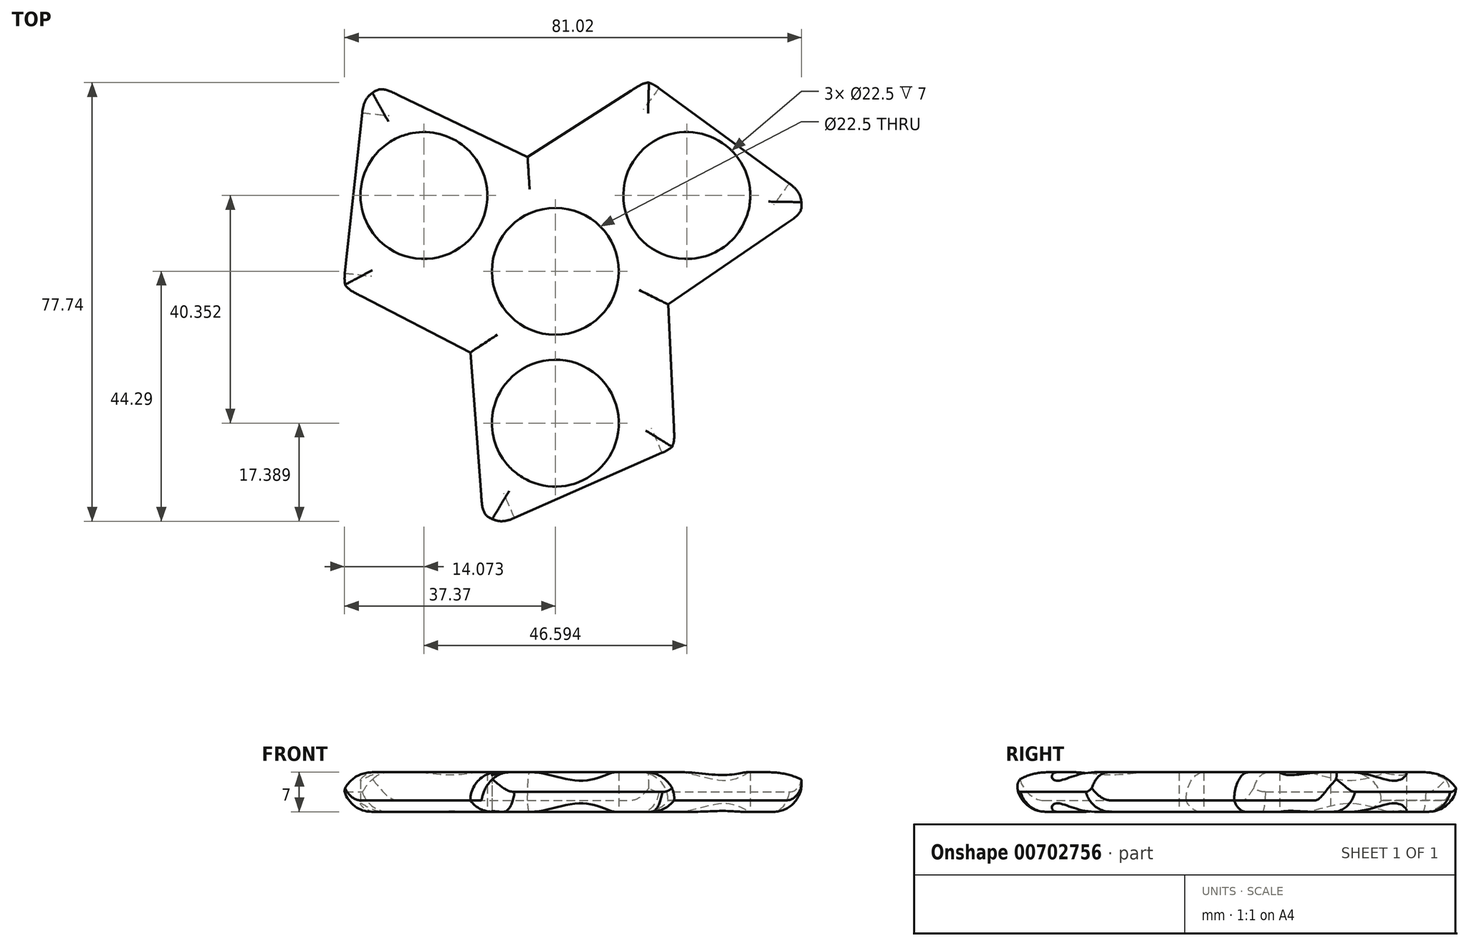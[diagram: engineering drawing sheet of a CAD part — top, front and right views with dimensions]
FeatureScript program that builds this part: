
annotation { "Feature Type Name" : "Feature", "Feature Type Description" : "" }
export const myFeature = defineFeature(function(context is Context, id is Id, definition is map)
    precondition{}
    {
        {
            var Q0;
            Q0=qCreatedBy(makeId("Top.planeOp"),FACE);
            var sketch = newSketch(context, id + "F0", { "sketchPlane" : qUnion([Q0])});
            skCircle(sketch, "E0", {"center": v(0, 0) * mm, "radius": 11.25 * mm});
            skLineSegment(sketch, "E1", {"start": v(19.99, -5.86) * mm, "end": v(21.2, -31.4) * mm});
            skCircle(sketch, "E2", {"center": v(0, -26.9) * mm, "radius": 11.25 * mm});
            skCircle(sketch, "E3.1.0", {"center": v(23.3, 13.45) * mm, "radius": 11.25 * mm});
            skLineSegment(sketch, "E3.1.1", {"start": v(-4.92, 20.24) * mm, "end": v(16.6, 34.06) * mm});
            skCircle(sketch, "E3.2.0", {"center": v(-23.3, 13.45) * mm, "radius": 11.25 * mm});
            skLineSegment(sketch, "E3.2.1", {"start": v(-15.07, -14.38) * mm, "end": v(-37.8, -2.65) * mm});
            skLineSegment(sketch, "E4", {"start": v(-37.8, -2.65) * mm, "end": v(-33.81, 34.11) * mm});
            skLineSegment(sketch, "E5.1.0", {"start": v(21.2, -31.4) * mm, "end": v(-12.64, -46.34) * mm});
            skLineSegment(sketch, "E5.2.0", {"start": v(16.6, 34.06) * mm, "end": v(46.45, 12.23) * mm});
            skLineSegment(sketch, "E6", {"start": v(-33.81, 34.11) * mm, "end": v(-4.92, 20.24) * mm});
            skLineSegment(sketch, "E7.1.0", {"start": v(-12.64, -46.34) * mm, "end": v(-15.07, -14.38) * mm});
            skLineSegment(sketch, "E7.2.0", {"start": v(46.45, 12.23) * mm, "end": v(19.99, -5.86) * mm});
            skSolve(sketch);
        }
        {
            var Q0;
            Q0 = qSketchRegion(id + "F0", true);
            extrude(context, id + "F1", {"entities" : qUnion([Q0]), "depth" : 7 * mm, "offsetDistance" : 25 * mm});
        }
        {
            var Q0;
            Q0=makeQuery(id+"F1.opExtrude","CAP_EDGE",EDGE,{"disambiguationData":[OSD([sQuery(id+"F0.wireOp",EDGE,"E4")])],"isStart":false});
            var Q1;
            Q1=makeQuery(id+"F1.opExtrude","CAP_EDGE",EDGE,{"disambiguationData":[OSD([sQuery(id+"F0.wireOp",EDGE,"E5.2.0")])],"isStart":false});
            var Q2;
            Q2=makeQuery(id+"F1.opExtrude","CAP_EDGE",EDGE,{"disambiguationData":[OSD([sQuery(id+"F0.wireOp",EDGE,"E5.1.0")])],"isStart":false});
            var Q3;
            Q3=makeQuery(id+"F1.opExtrude","CAP_EDGE",EDGE,{"disambiguationData":[OSD([sQuery(id+"F0.wireOp",EDGE,"E5.1.0")])],"isStart":true});
            var Q4;
            Q4=makeQuery(id+"F1.opExtrude","CAP_EDGE",EDGE,{"disambiguationData":[OSD([sQuery(id+"F0.wireOp",EDGE,"E4")])],"isStart":true});
            var Q5;
            Q5=makeQuery(id+"F1.opExtrude","CAP_EDGE",EDGE,{"disambiguationData":[OSD([sQuery(id+"F0.wireOp",EDGE,"E5.2.0")])],"isStart":true});
            fillet(context, id + "F2", {"entities" : qUnion([Q0, Q1, Q2, Q3, Q4, Q5]), "radius" : 5 * mm, "tangentPropagation" : true, "allowEdgeOverflow" : false});
        }
        {
            var Q0;
            Q0=makeQuery(id+"F1.opExtrude","CAP_EDGE",EDGE,{"disambiguationData":[OSD([sQuery(id+"F0.wireOp",EDGE,"E6")])],"isStart":false});
            var Q1;
            Q1=makeQuery(id+"F1.opExtrude","CAP_EDGE",EDGE,{"disambiguationData":[OSD([sQuery(id+"F0.wireOp",EDGE,"E3.1.1")])],"isStart":false});
            var Q2;
            Q2=makeQuery(id+"F1.opExtrude","CAP_EDGE",EDGE,{"disambiguationData":[OSD([sQuery(id+"F0.wireOp",EDGE,"E7.2.0")])],"isStart":false});
            var Q3;
            Q3=makeQuery(id+"F1.opExtrude","CAP_EDGE",EDGE,{"disambiguationData":[OSD([sQuery(id+"F0.wireOp",EDGE,"E1")])],"isStart":false});
            var Q4;
            Q4=makeQuery(id+"F1.opExtrude","CAP_EDGE",EDGE,{"disambiguationData":[OSD([sQuery(id+"F0.wireOp",EDGE,"E7.1.0")])],"isStart":false});
            var Q5;
            Q5=makeQuery(id+"F1.opExtrude","CAP_EDGE",EDGE,{"disambiguationData":[OSD([sQuery(id+"F0.wireOp",EDGE,"E3.2.1")])],"isStart":false});
            fillet(context, id + "F3", {"entities" : qUnion([Q0, Q1, Q2, Q3, Q4, Q5]), "radius" : 5 * mm, "tangentPropagation" : true, "allowEdgeOverflow" : false});
        }
        {
            var Q0;
            Q0=makeQuery(id+"F1.opExtrude","CAP_EDGE",EDGE,{"disambiguationData":[OSD([sQuery(id+"F0.wireOp",EDGE,"E1")])],"isStart":true});
            var Q1;
            Q1=makeQuery(id+"F1.opExtrude","CAP_EDGE",EDGE,{"disambiguationData":[OSD([sQuery(id+"F0.wireOp",EDGE,"E7.2.0")])],"isStart":true});
            var Q2;
            Q2=makeQuery(id+"F1.opExtrude","CAP_EDGE",EDGE,{"disambiguationData":[OSD([sQuery(id+"F0.wireOp",EDGE,"E3.1.1")])],"isStart":true});
            var Q3;
            Q3=makeQuery(id+"F1.opExtrude","CAP_EDGE",EDGE,{"disambiguationData":[OSD([sQuery(id+"F0.wireOp",EDGE,"E6")])],"isStart":true});
            var Q4;
            Q4=makeQuery(id+"F1.opExtrude","CAP_EDGE",EDGE,{"disambiguationData":[OSD([sQuery(id+"F0.wireOp",EDGE,"E3.2.1")])],"isStart":true});
            var Q5;
            Q5=makeQuery(id+"F1.opExtrude","CAP_EDGE",EDGE,{"disambiguationData":[OSD([sQuery(id+"F0.wireOp",EDGE,"E7.1.0")])],"isStart":true});
            fillet(context, id + "F4", {"entities" : qUnion([Q0, Q1, Q2, Q3, Q4, Q5]), "radius" : 5 * mm, "tangentPropagation" : true, "allowEdgeOverflow" : false});
        }
    });
